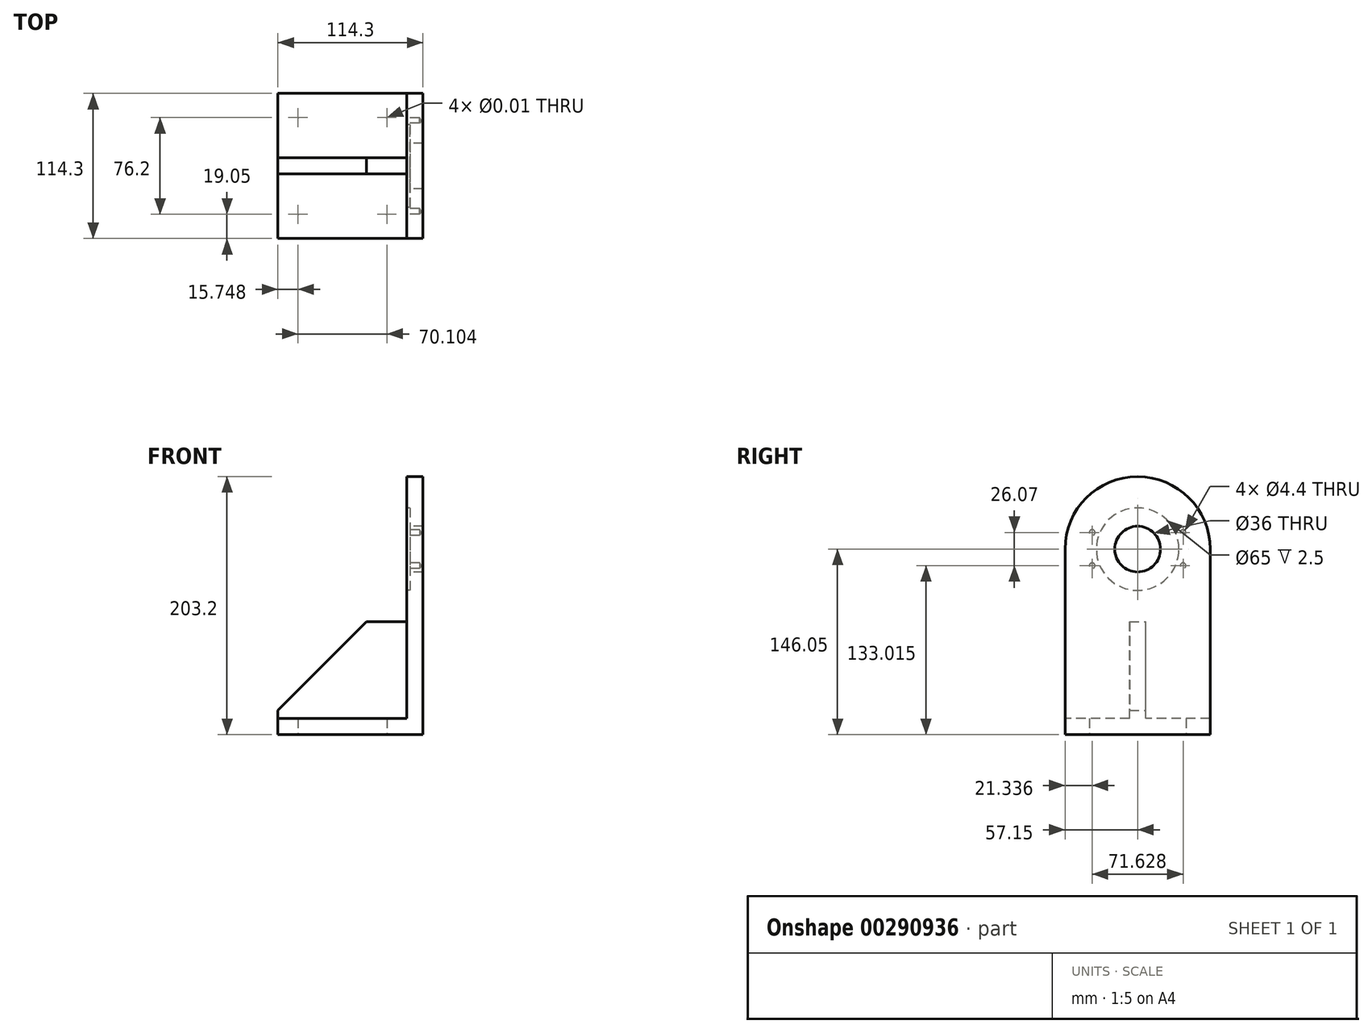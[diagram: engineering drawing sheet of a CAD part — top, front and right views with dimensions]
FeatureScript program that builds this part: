
annotation { "Feature Type Name" : "Feature", "Feature Type Description" : "" }
export const myFeature = defineFeature(function(context is Context, id is Id, definition is map)
    precondition{}
    {
        {
            var Q0;
            Q0=qCreatedBy(makeId("Right.planeOp"),FACE);
            var sketch = newSketch(context, id + "F0", { "sketchPlane" : qUnion([Q0])});
            skArc(sketch, "E0", {"start": v(57.15, 0) * mm, "mid": v(0, 57.15) * mm, "end": v(-57.15, 0) * mm});
            skLineSegment(sketch, "E1", {"start": v(-116.92, 0) * mm, "end": v(108.36, 0) * mm, "construction": true});
            skLineSegment(sketch, "E2.0", {"start": v(-116.92, -146.05) * mm, "end": v(108.36, -146.05) * mm, "construction": true});
            skLineSegment(sketch, "E3", {"start": v(-57.15, 0) * mm, "end": v(-57.15, -146.05) * mm});
            skLineSegment(sketch, "E4", {"start": v(57.15, 0) * mm, "end": v(57.15, -146.05) * mm});
            skLineSegment(sketch, "E5", {"start": v(-57.15, -146.05) * mm, "end": v(57.15, -146.05) * mm});
            skSolve(sketch);
        }
        {
            var Q0;
            Q0 = qSketchRegion(id + "F0", true);
            extrude(context, id + "F1", {"entities" : qUnion([Q0]), "depth" : 12.7 * mm});
        }
        {
            var Q0;
            Q0=sQuery(id+"F0.wireOp",VERTEX,"E0.center");
            var Q1;
            Q1=makeQuery(id+"F1.opExtrude","SWEPT_BODY",BODY,{"disambiguationData":[OSD([sQuery(id+"F0.wireOp",EDGE,"E0"),sQuery(id+"F0.wireOp",EDGE,"E3"),sQuery(id+"F0.wireOp",EDGE,"E4"),sQuery(id+"F0.wireOp",EDGE,"E5")])]});
            hole(context, id + "F2", {"style" : HoleStyle.C_BORE, "endStyle" : HoleEndStyle.BLIND, "oppositeDirection" : true, "holeDiameter" : 36 * mm, "cBoreDiameter" : 65 * mm, "cBoreDepth" : 2.5 * mm, "holeDepth" : 36 * mm, "tappedDepth" : 12.7 * mm, "tapClearance" : 3, "locations" : qUnion([Q0]), "scope" : qUnion([Q1])});
        }
        {
            var Q0;
            Q0=makeQuery(id+"F0.imprint","IMPRINT",FACE,{"disambiguationData":[TD([[makeQuery(id+"F0.imprint","IMPRINT",EDGE,{"derivedFrom":sQuery(id+"F0.wireOp",EDGE,"E0")}),1.0]])]});
            var sketch = newSketch(context, id + "F3", { "sketchPlane" : qUnion([Q0])});
            skLineSegment(sketch, "E6", {"start": v(0, 0) * mm, "end": v(103.43, 37.65) * mm, "construction": true});
            skLineSegment(sketch, "E7", {"start": v(0, 0) * mm, "end": v(101.55, -36.96) * mm, "construction": true});
            skLineSegment(sketch, "E8", {"start": v(0, 113.02) * mm, "end": v(0, -176.89) * mm, "construction": true});
            skLineSegment(sketch, "E9.0", {"start": v(35.81, 113.02) * mm, "end": v(35.81, -176.89) * mm, "construction": true});
            skPoint(sketch, "E10", {"position": v(35.81, 13.04) * mm});
            skPoint(sketch, "E11", {"position": v(35.81, -13.04) * mm});
            skPoint(sketch, "E12.MirrorP", {"position": v(-35.81, 13.04) * mm});
            skPoint(sketch, "E13.MirrorP", {"position": v(-35.81, -13.04) * mm});
            skSolve(sketch);
        }
        {
            var Q0;
            Q0=sQuery(id+"F3.wireOp",VERTEX,"E10");
            var Q1;
            Q1=sQuery(id+"F3.wireOp",VERTEX,"E11");
            var Q2;
            Q2=sQuery(id+"F3.wireOp",VERTEX,"E12.MirrorP");
            var Q3;
            Q3=sQuery(id+"F3.wireOp",VERTEX,"E13.MirrorP");
            var Q4;
            Q4=makeQuery(id+"F1.opExtrude","SWEPT_BODY",BODY,{"disambiguationData":[OSD([sQuery(id+"F0.wireOp",EDGE,"E0"),sQuery(id+"F0.wireOp",EDGE,"E3"),sQuery(id+"F0.wireOp",EDGE,"E4"),sQuery(id+"F0.wireOp",EDGE,"E5")])]});
            hole(context, id + "F4", {"style" : HoleStyle.SIMPLE, "endStyle" : HoleEndStyle.BLIND, "oppositeDirection" : true, "standardTappedOrClearance" : lookupTablePath({ "standard" : "ISO", "fit" : "Normal", "size" : "M4", "type" : "Clearance" }), "standardBlindInLast" : lookupTablePath({ "fit" : "Standard", "standard" : "ISO", "size" : "M4", "type" : "Clearance" }), "holeDiameter" : 4.4 * mm, "holeDepth" : 10 * mm, "tappedDepth" : 12.7 * mm, "tapClearance" : 3, "locations" : qUnion([Q0, Q1, Q2, Q3]), "scope" : qUnion([Q4])});
        }
        {
            var Q0;
            Q0=makeQuery(id+"F0.imprint","IMPRINT",FACE,{"disambiguationData":[TD([[makeQuery(id+"F0.imprint","IMPRINT",EDGE,{"derivedFrom":sQuery(id+"F0.wireOp",EDGE,"E0")}),1.0]])]});
            var sketch = newSketch(context, id + "F5", { "sketchPlane" : qUnion([Q0])});
            skLineSegment(sketch, "E14.0", {"start": v(-57.15, -146.05) * mm, "end": v(57.15, -146.05) * mm, "construction": true});
            skLineSegment(sketch, "E15.bottom", {"start": v(57.15, -146.05) * mm, "end": v(-57.15, -146.05) * mm});
            skLineSegment(sketch, "E15.top", {"start": v(57.15, -133.35) * mm, "end": v(-57.15, -133.35) * mm});
            skLineSegment(sketch, "E15.left", {"start": v(57.15, -146.05) * mm, "end": v(57.15, -133.35) * mm});
            skLineSegment(sketch, "E15.right", {"start": v(-57.15, -146.05) * mm, "end": v(-57.15, -133.35) * mm});
            skSolve(sketch);
        }
        {
            var Q0;
            Q0 = qSketchRegion(id + "F5", true);
            extrude(context, id + "F6", {"entities" : qUnion([Q0]), "operationType" : NewBodyOperationType.ADD, "oppositeDirection" : true, "depth" : 101.6 * mm});
        }
        {
            var Q0;
            Q0=qCreatedBy(makeId("Front.planeOp"),FACE);
            var sketch = newSketch(context, id + "F7", { "sketchPlane" : qUnion([Q0])});
            skLineSegment(sketch, "E16.0", {"start": v(0, 0) * mm, "end": v(0, -146.05) * mm, "construction": true});
            skLineSegment(sketch, "E17.0", {"start": v(-101.6, -133.35) * mm, "end": v(0, -133.35) * mm, "construction": true});
            skLineSegment(sketch, "E18.bottom", {"start": v(-101.6, -133.35) * mm, "end": v(0, -133.35) * mm});
            skLineSegment(sketch, "E18.top", {"start": v(-101.6, -57.15) * mm, "end": v(0, -57.15) * mm});
            skLineSegment(sketch, "E18.left", {"start": v(-101.6, -133.35) * mm, "end": v(-101.6, -57.15) * mm});
            skLineSegment(sketch, "E18.right", {"start": v(0, -133.35) * mm, "end": v(0, -57.15) * mm});
            skSolve(sketch);
        }
        {
            var Q0;
            Q0 = qSketchRegion(id + "F7", true);
            extrude(context, id + "F8", {"entities" : qUnion([Q0]), "operationType" : NewBodyOperationType.ADD, "endBound" : BoundingType.SYMMETRIC, "depth" : 12.7 * mm});
        }
        {
            var Q0;
            Q0=makeQuery(id+"F8.opExtrude","SWEPT_EDGE",EDGE,{"disambiguationData":[OSD([sQuery(id+"F7.wireOp",EDGE,"E18.top"),sQuery(id+"F7.wireOp",EDGE,"E18.left")])]});
            chamfer(context, id + "F9", {"entities" : qUnion([Q0]), "width" : 69.85 * mm, "tangentPropagation" : true});
        }
        {
            var Q0;
            Q0=makeQuery(id+"F6.boolean.opBoolean","MERGE",FACE,{"derivedFrom":[makeQuery(id+"F1.opExtrude","SWEPT_FACE",FACE,{"disambiguationData":[OSD([sQuery(id+"F0.wireOp",EDGE,"E5")])]}),makeQuery(id+"F6.opExtrude","SWEPT_FACE",FACE,{"disambiguationData":[OSD([sQuery(id+"F5.wireOp",EDGE,"E15.bottom")])]})]});
            var sketch = newSketch(context, id + "F10", { "sketchPlane" : qUnion([Q0])});
            skLineSegment(sketch, "E19.0", {"start": v(-101.6, 57.15) * mm, "end": v(-101.6, -57.15) * mm, "construction": true});
            skLineSegment(sketch, "E20", {"start": v(-101.6, 0) * mm, "end": v(0, 0) * mm, "construction": true});
            skLineSegment(sketch, "E21.0", {"start": v(0, 116.92) * mm, "end": v(0, -108.36) * mm, "construction": true});
            skLineSegment(sketch, "E22", {"start": v(-50.8, -92.1) * mm, "end": v(-50.8, 90.86) * mm, "construction": true});
            skPoint(sketch, "E23.orphan", {"position": v(-50.8, 0) * mm});
            skLineSegment(sketch, "E24.0", {"start": v(-101.6, 38.1) * mm, "end": v(0, 38.1) * mm, "construction": true});
            skLineSegment(sketch, "E25.0", {"start": v(-85.85, -92.1) * mm, "end": v(-85.85, 90.86) * mm, "construction": true});
            skPoint(sketch, "E26", {"position": v(-85.85, 38.1) * mm});
            skPoint(sketch, "E27.MirrorP", {"position": v(-15.75, 38.1) * mm});
            skPoint(sketch, "E28.MirrorP", {"position": v(-85.85, -38.1) * mm});
            skPoint(sketch, "E29.MirrorP", {"position": v(-15.75, -38.1) * mm});
            skSolve(sketch);
        }
        {
            var Q0;
            Q0=sQuery(id+"F10.wireOp",VERTEX,"E26");
            var Q1;
            Q1=sQuery(id+"F10.wireOp",VERTEX,"E27.MirrorP");
            var Q2;
            Q2=sQuery(id+"F10.wireOp",VERTEX,"E28.MirrorP");
            var Q3;
            Q3=sQuery(id+"F10.wireOp",VERTEX,"E29.MirrorP");
            var Q4;
            Q4=makeQuery(id+"F1.opExtrude","SWEPT_BODY",BODY,{"disambiguationData":[OSD([sQuery(id+"F0.wireOp",EDGE,"E0"),sQuery(id+"F0.wireOp",EDGE,"E3"),sQuery(id+"F0.wireOp",EDGE,"E4"),sQuery(id+"F0.wireOp",EDGE,"E5")])]});
            hole(context, id + "F11", {"style" : HoleStyle.SIMPLE, "endStyle" : HoleEndStyle.THROUGH, "standardTappedOrClearance" : lookupTablePath({ "standard" : "ANSI", "size" : "5/16 (0.31)", "type" : "Drilled" }), "standardBlindInLast" : lookupTablePath({ "standard" : "ANSI", "size" : "5/16", "type" : "Drilled" }), "holeDiameter" : 5 / 406.4 * mm, "tappedDepth" : 12.7 * mm, "tapClearance" : 3, "locations" : qUnion([Q0, Q1, Q2, Q3]), "scope" : qUnion([Q4])});
        }
    });
